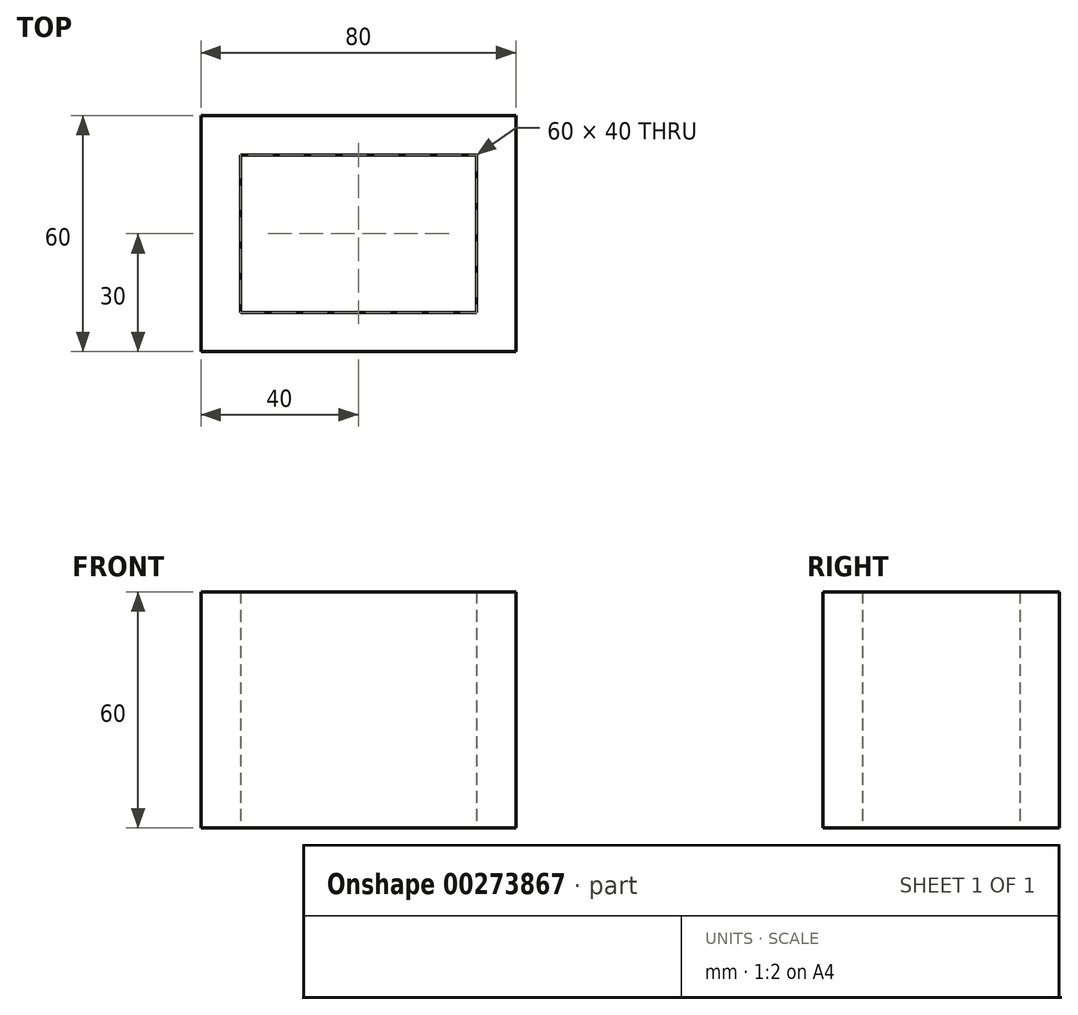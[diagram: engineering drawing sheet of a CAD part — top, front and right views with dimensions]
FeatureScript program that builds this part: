
annotation { "Feature Type Name" : "Feature", "Feature Type Description" : "" }
export const myFeature = defineFeature(function(context is Context, id is Id, definition is map)
    precondition{}
    {
        {
            var Q0;
            Q0=qCreatedBy(makeId("Top.planeOp"),FACE);
            var sketch = newSketch(context, id + "F0", { "sketchPlane" : qUnion([Q0])});
            skLineSegment(sketch, "E0.bottom", {"start": v(0, 0) * mm, "end": v(80, 0) * mm});
            skLineSegment(sketch, "E0.top", {"start": v(0, 60) * mm, "end": v(80, 60) * mm});
            skLineSegment(sketch, "E0.left", {"start": v(0, 0) * mm, "end": v(0, 60) * mm});
            skLineSegment(sketch, "E0.right", {"start": v(80, 0) * mm, "end": v(80, 60) * mm});
            skLineSegment(sketch, "E1.bottom", {"start": v(10, 50) * mm, "end": v(70, 50) * mm});
            skLineSegment(sketch, "E1.top", {"start": v(10, 10) * mm, "end": v(70, 10) * mm});
            skLineSegment(sketch, "E1.left", {"start": v(10, 50) * mm, "end": v(10, 10) * mm});
            skLineSegment(sketch, "E1.right", {"start": v(70, 50) * mm, "end": v(70, 10) * mm});
            skSolve(sketch);
        }
        {
            var Q0;
            Q0 = qSketchRegion(id + "F0", true);
            extrude(context, id + "F1", {"entities" : qUnion([Q0]), "endBound" : BoundingType.SYMMETRIC, "depth" : 60 * mm});
        }
    });
